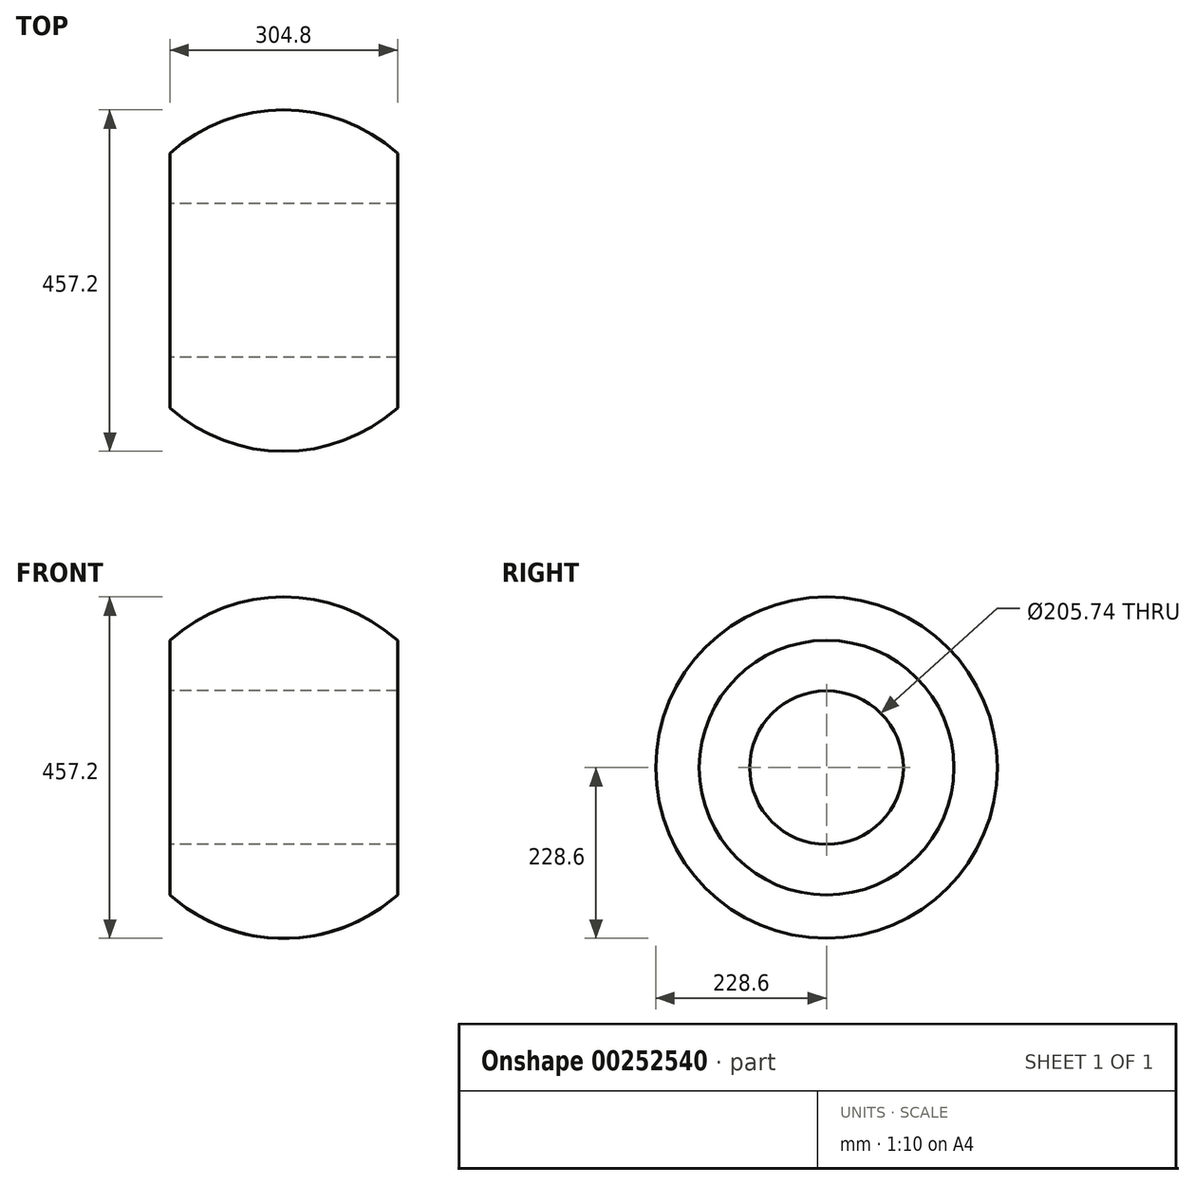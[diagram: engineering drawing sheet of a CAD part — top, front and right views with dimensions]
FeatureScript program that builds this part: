
annotation { "Feature Type Name" : "Feature", "Feature Type Description" : "" }
export const myFeature = defineFeature(function(context is Context, id is Id, definition is map)
    precondition{}
    {
        {
            var Q0;
            Q0=qCreatedBy(makeId("Top.planeOp"),FACE);
            var sketch = newSketch(context, id + "F0", { "sketchPlane" : qUnion([Q0])});
            skLineSegment(sketch, "E0", {"start": v(-76.2, 0) * mm, "end": v(-381, 0) * mm});
            skArc(sketch, "E1", {"start": v(-76.2, 170.39) * mm, "mid": v(-228.6, 228.6) * mm, "end": v(-381, 170.39) * mm});
            skLineSegment(sketch, "E2", {"start": v(-381, 0) * mm, "end": v(-381, 170.39) * mm});
            skLineSegment(sketch, "E3", {"start": v(-76.2, 0) * mm, "end": v(-76.2, 170.39) * mm});
            skPoint(sketch, "E4.orphan", {"position": v(-457.2, 0) * mm});
            skPoint(sketch, "E5.orphan", {"position": v(0, 0) * mm});
            skSolve(sketch);
        }
        {
            var Q0;
            Q0=makeQuery(id+"F0.imprint","IMPRINT",FACE,{"disambiguationData":[TD([[makeQuery(id+"F0.imprint","IMPRINT",EDGE,{"derivedFrom":sQuery(id+"F0.wireOp",EDGE,"E0")}),-1.0]])]});
            var Q1;
            Q1=sQuery(id+"F0.wireOp",EDGE,"E0");
            revolve(context, id + "F1", {"entities" : qUnion([Q0]), "axis" : qUnion([Q1]), "revolveType" : RevolveType.FULL});
        }
        {
            var Q0;
            Q0=makeQuery(id+"F1.opRevolve","SWEPT_FACE",FACE,{"disambiguationData":[OSD([sQuery(id+"F0.wireOp",EDGE,"E2")])]});
            var sketch = newSketch(context, id + "F2", { "sketchPlane" : qUnion([Q0])});
            skCircle(sketch, "E6", {"center": v(0, 0) * mm, "radius": 102.87 * mm});
            skSolve(sketch);
        }
        {
            var Q0;
            Q0=makeQuery(id+"F2.imprint","IMPRINT",FACE,{"disambiguationData":[TD([[makeQuery(id+"F2.imprint","IMPRINT",EDGE,{"derivedFrom":sQuery(id+"F2.wireOp",EDGE,"E6")}),1.0]])]});
            extrude(context, id + "F3", {"entities" : qUnion([Q0]), "operationType" : NewBodyOperationType.REMOVE, "endBound" : BoundingType.THROUGH_ALL, "oppositeDirection" : true, "depth" : 25.4 * mm});
        }
    });
